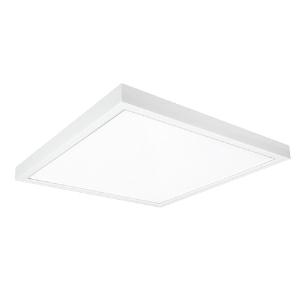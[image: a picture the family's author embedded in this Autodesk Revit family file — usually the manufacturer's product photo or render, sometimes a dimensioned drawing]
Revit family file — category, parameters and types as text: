
# Revit family: 3f_filippi_-_p_250_luce_diffusa_lgs_3f_filippi_-_10049_-_p_250_28w_led_dali_lgs_596x596
name_source: partatom
category: Lighting Fixtures
units: mm (PartAtom-declared; Revit-internal decimal feet)

## family parameters
Cut with Voids When Loaded = No
Host = Face
Light Source = No
Part Type = Normal
Room Calculation Point = No
Round Connector Dimension = Use Diameter
Shared = No

## types (1)
- 3F Filippi - P 250 Luce Diffusa LGS (1 x LED, 3707 lm, 31 W, 4000 K)
    Apparent Load = 31 VA
    Approval mark = ENEC
    CIE Flux Codes = 66 93 99 100 100
    Color Rendering = 80
    Color Temperature = 4000 K
    Control Gear = Electronic transformer
    Default Elevation = 1800 mm
    Description = ILLUMINOTECHNICAL
Luminous efficiency 100% (DLOR 100%, ULOR 0%).
Initial luminous flux of the luminaire 3707 lm.
Direct symmetric distribution.
Installation Interdistance Transv.D = 1.18 x hu - Long.D = 1.17 x hu.
Average luminance <1500 cd/m² for radial angles >65°.
Tabular UGR (CIE 117 - 4H-8H; S=0.25H; 70/50/20): RUG 16.5 - 16.5.
Beam angle: 87° - 86°.
Luminous efficacy 120 lm/W.
Lifetime (L93/B10): 30000 h. (tq+25°C)
Lifetime (L90/B10): 50000 h. (tq+25°C)
Lifetime (L85/B10): 80000 h. (tq+25°C)
Lifetime (L80/B10): 100000 h. (tq+25°C)
Sudden decreased luminous flux after 50000 hours: 0% (C0).
Photobiological safety in compliance with IEC/TR 62778: RG0 risk exempt, (IEC 62471).
In compliance with IEC/EN 62722-2-1 - IEC/EN 62717 standards.

SOURCE
Squared LED module 28W/840.
Energy efficiency class (UE 2019/2020 - UE 2019/2015): D.
CIE 13.3 Colour rendering index: CRI >80 (R9 <50%).
IES TM-30 Fidelity Index: Rf = 84 Rg = 95.
CCT nominal colour temperature 4000 K.
Colour initial tolerance (MacAdam): SDCM 3.

MECHANICAL
Housing in galvannealed steel, painted in white epoxy-polyester.
Height only 55 mm.
LGS micro-prismatic flat diffuser in transparent methacrylate (PMMA), multi-lenticular exterior, anti-glare, locked to the white painted aluminium perimeter frame, hinged opening.
Anti-glare opal polycarbonate filter for brightness uniformity.
Luminaire with limited surface temperature. - D - (EN 60598-2-24)
Dimensions: 596x596 mm, height 55 mm. Weight 5.35 kg.
IP40 protection degree.
Mechanical strength to impacts IK06 (1 joule).
Glow-wire test resistance 650°C.

ELECTRICAL
Halogen Free DALI-2 DATI (Parts 251, 252, 253), PUSH-DIM, electronic wiring 230V-50/60Hz, power factor 0.95 at full load, THD <25%, constant output current, SELV, class I, 1 driver, 1 DALI addresse.
Power of the luminaire 31 W.
CE - IEC 60598-1 - EN 60598-1.
SAFE FLICKER: PstLM=<1 and SVM=<0.4 (IEC TR 61547-1 and IEC TR 63158), to ensure a more comfortable and safe light.
Luminaire compliant with EN 60598-2-22 for power supply from a centralised emergency system CPSS (Central Power Supply System), not incorporated in the luminaire - high risk areas excluded. The default power and flux are 100% in AC and 15% in DC.
Ambient temperature from 0°C to +25°C.
Temperature class T6 max 85°C.
Relative humidity UR: <85%.

INSTALLATION
Ceiling.
All accessories dedicated to this product are available on the Catalog and on our website www.3F-Filippi.com.

APPLICATIONS
Particularly suitable for low height environments.
Environments: with video terminals, representative areas, offices.
Environments with exacting visual tasks, where diffused soft light for optimum visual comfort is required.

LIGHT MANAGEMENT
Recommended minimum setting: 10%.
The luminaire, equipped with (DALI-2 DATI) driver, can be controlled manually with 3F Easy Dim technology or automatically/manually with wired or wireless DALI/D2D control systems.
The D2D driver guarantees interoperability with other devices with the same certification by making the following information available:
Device Data (Part 251), Energy Report (Part 252), Diagnosis & Maintenance (Part 253).
In electrical systems without a regulation system (manual or automatic) and DALI bus, a suitable jumper must be made on the DA-DA terminals of the appliance.

WARNING
Luminaire designed for disposal/recycling at end-of-life.
Replaceable (LED only) light source by a professional. Replaceable control gear by a professional.
    Height = 55 mm
    Lamp = 1 x LED
    Lamp Light Flux = 3707 lm
    Lamp Power = 31 W
    Lamp count = 1
    Length = 596 mm
    Lifetime = 50000 h
    Luminous efficacy = 120 lm/W
    Manufacturer = 3F Filippi
    ModVariant = No
    Model = 3F Filippi - 10049 - P 250 28W LED DALI LGS 596x596
    Mounting Place = Ceiling
    Mounting Type = Surface mounted
    Number of Poles = 1
    OnlyDefault = Yes
    Power Factor = 1
    Product Name = 3F Filippi - P 250 Luce Diffusa LGS
    Product group = ceiling mounted luminaire
    ProductGroupID = 3
    Protection Class = Protection class I
    Protection Degree = IP 40
    RLX_Detail_Level = 1
    RLX_Emergency_Light_Flux = 0 lm
    RLX_Emergency_Type = 0
    RLX_Emergency_Type_DB = No
    RlxData = <blob elided: 36833 chars, md5=4a240336>
    Socket = socket
    Standby Power = 0 W
    System Light Flux = 3707 lm
    System Power = 31 W
    Type Comments = Product without accessories
    Type Image = 3ffilippi_p_250_led_luce_diffusa_lgs.jpg
    URL = http://relux.com
    VarID = ---
    Voltage = 0 V
    Weight = 0.00 kg
    Width = 596 mm

## geometry (parser evidence)
native form markers: Blend x4, Sweep x10
no freeform markers — native parametric forms only
